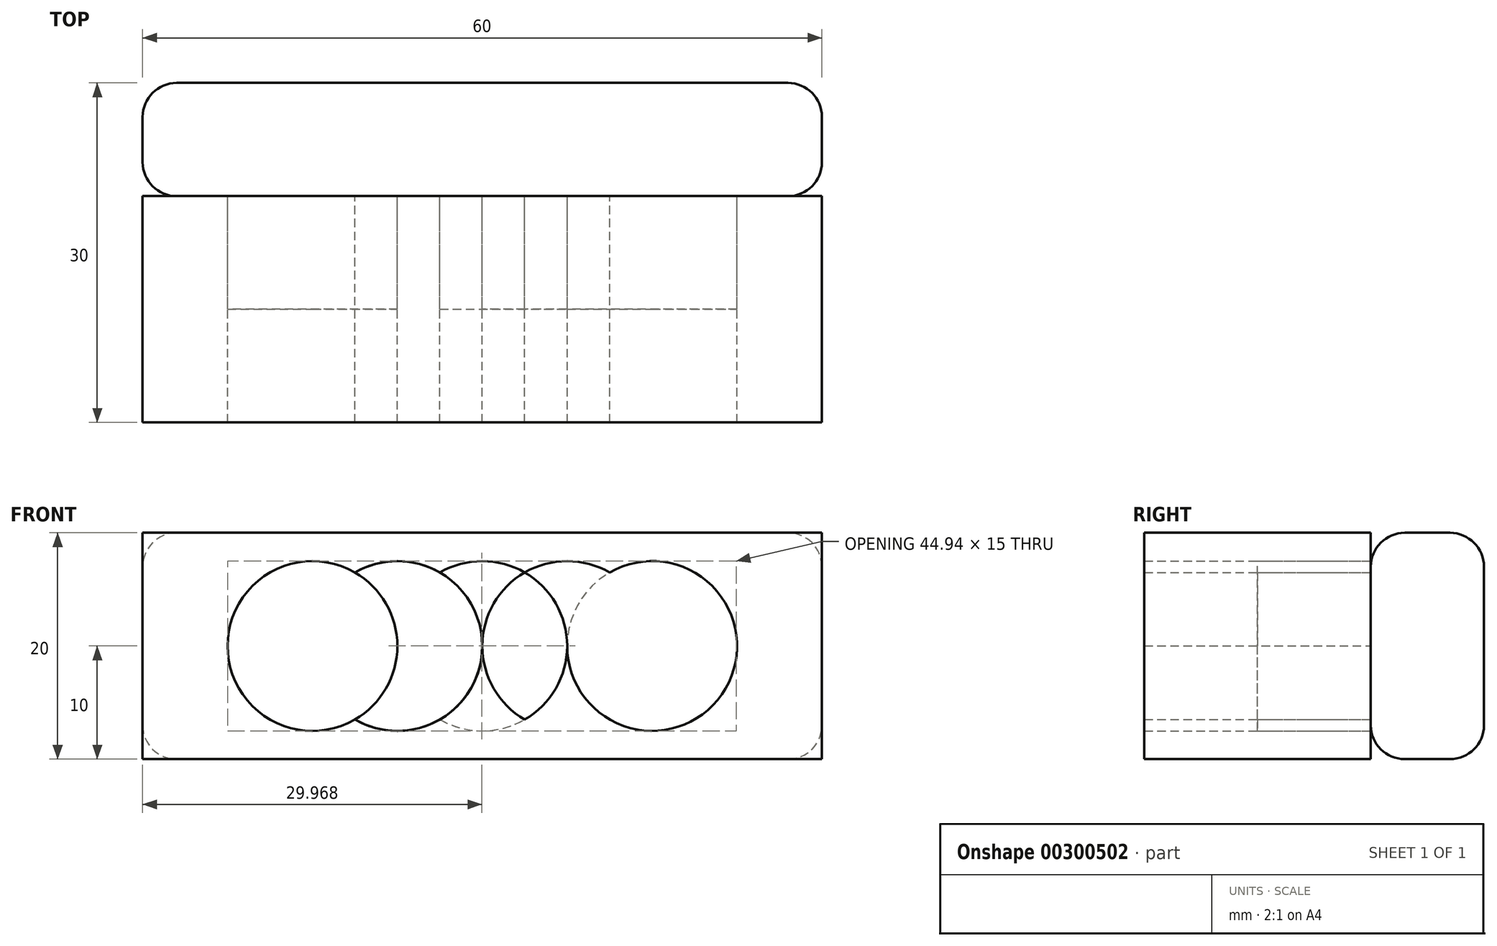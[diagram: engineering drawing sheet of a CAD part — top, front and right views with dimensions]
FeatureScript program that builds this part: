
annotation { "Feature Type Name" : "Feature", "Feature Type Description" : "" }
export const myFeature = defineFeature(function(context is Context, id is Id, definition is map)
    precondition{}
    {
        {
            var Q0;
            Q0=qCreatedBy(makeId("Front.planeOp"),FACE);
            var sketch = newSketch(context, id + "F0", { "sketchPlane" : qUnion([Q0])});
            skLineSegment(sketch, "E0.bottom", {"start": v(-30, 10) * mm, "end": v(30, 10) * mm});
            skLineSegment(sketch, "E0.top", {"start": v(-30, -10) * mm, "end": v(30, -10) * mm});
            skLineSegment(sketch, "E0.left", {"start": v(-30, 10) * mm, "end": v(-30, -10) * mm});
            skLineSegment(sketch, "E0.right", {"start": v(30, 10) * mm, "end": v(30, -10) * mm});
            skPoint(sketch, "E0.middle", {"position": v(0, 0) * mm});
            skSolve(sketch);
        }
        {
            var Q0;
            Q0=makeQuery(id+"F0.imprint","IMPRINT",FACE,{"disambiguationData":[TD([[makeQuery(id+"F0.imprint","IMPRINT",EDGE,{"derivedFrom":sQuery(id+"F0.wireOp",EDGE,"E0.bottom")}),-1.0]])]});
            extrude(context, id + "F1", {"entities" : qUnion([Q0]), "depth" : 10 * mm});
        }
        {
            var Q0;
            Q0=makeQuery(id+"F1.opExtrude","CAP_FACE",FACE,{"disambiguationData":[OSD([sQuery(id+"F0.wireOp",EDGE,"E0.bottom"),sQuery(id+"F0.wireOp",EDGE,"E0.top"),sQuery(id+"F0.wireOp",EDGE,"E0.left"),sQuery(id+"F0.wireOp",EDGE,"E0.right")])],"isStart":false});
            var sketch = newSketch(context, id + "F2", { "sketchPlane" : qUnion([Q0])});
            skCircle(sketch, "E1", {"center": v(0, 0) * mm, "radius": 7.5 * mm});
            skCircle(sketch, "E2", {"center": v(-7.5, 0) * mm, "radius": 7.5 * mm});
            skCircle(sketch, "E3", {"center": v(7.5, 0) * mm, "radius": 7.5 * mm});
            skCircle(sketch, "E4", {"center": v(15, 0) * mm, "radius": 7.5 * mm});
            skCircle(sketch, "E5", {"center": v(-15, 0) * mm, "radius": 7.5 * mm});
            skSolve(sketch);
        }
        {
            var Q0;
            {var subQ0=sQuery(id+"F2.wireOp",EDGE,"E5");var subQ1=sQuery(id+"F2.wireOp",EDGE,"E2");var subQ2=makeQuery(id+"F2.imprint","INTERSECT",VERTEX,{"disambiguationData":[OD(0.0)],"derivedFrom":[subQ1,subQ0]});Q0=makeQuery(id+"F2.imprint","IMPRINT",FACE,{"disambiguationData":[TD([[makeQuery(id+"F2.imprint","IMPRINT",EDGE,{"disambiguationData":[TD([[subQ2,-1.0]])],"derivedFrom":subQ1}),-1.0]])]});}
            var Q1;
            {var subQ0=sQuery(id+"F2.wireOp",EDGE,"E5");var subQ1=sQuery(id+"F2.wireOp",EDGE,"E2");var subQ2=makeQuery(id+"F2.imprint","INTERSECT",VERTEX,{"disambiguationData":[OD(0.0)],"derivedFrom":[subQ1,subQ0]});Q1=makeQuery(id+"F2.imprint","IMPRINT",FACE,{"disambiguationData":[TD([[makeQuery(id+"F2.imprint","IMPRINT",EDGE,{"disambiguationData":[TD([[subQ2,-1.0]])],"derivedFrom":subQ1}),1.0]])]});}
            var Q2;
            Q2=sQuery(id+"F2.wireOp",EDGE,"E5");
            var Q3;
            Q3=sQuery(id+"F2.wireOp",EDGE,"E4");
            extrude(context, id + "F3", {"entities" : qUnion([Q0, Q1]), "surfaceEntities" : qUnion([Q2, Q3]), "depth" : 10 * mm});
        }
        {
            var Q0;
            {var subQ0=sQuery(id+"F2.wireOp",EDGE,"E2");var subQ1=sQuery(id+"F2.wireOp",EDGE,"E1");var subQ2=makeQuery(id+"F2.imprint","INTERSECT",VERTEX,{"disambiguationData":[OD(0.0)],"derivedFrom":[subQ1,subQ0]});Q0=makeQuery(id+"F2.imprint","IMPRINT",FACE,{"disambiguationData":[TD([[makeQuery(id+"F2.imprint","IMPRINT",EDGE,{"disambiguationData":[TD([[subQ2,-1.0]])],"derivedFrom":subQ1}),1.0]])]});}
            var Q1;
            {var subQ0=sQuery(id+"F2.wireOp",EDGE,"E5");var subQ1=sQuery(id+"F2.wireOp",EDGE,"E1");var subQ2=makeQuery(id+"F2.imprint","INTERSECT",VERTEX,{"derivedFrom":[subQ1,subQ0]});Q1=makeQuery(id+"F2.imprint","IMPRINT",FACE,{"disambiguationData":[TD([[makeQuery(id+"F2.imprint","IMPRINT",EDGE,{"disambiguationData":[TD([[subQ2,-1.0]])],"derivedFrom":subQ1}),-1.0]])]});}
            var Q2;
            {var subQ0=sQuery(id+"F2.wireOp",EDGE,"E2");var subQ1=sQuery(id+"F2.wireOp",EDGE,"E1");var subQ2=makeQuery(id+"F2.imprint","INTERSECT",VERTEX,{"disambiguationData":[OD(0.0)],"derivedFrom":[subQ1,subQ0]});Q2=makeQuery(id+"F2.imprint","IMPRINT",FACE,{"disambiguationData":[TD([[makeQuery(id+"F2.imprint","IMPRINT",EDGE,{"disambiguationData":[TD([[subQ2,-1.0]])],"derivedFrom":subQ1}),-1.0]])]});}
            var Q3;
            Q3=sQuery(id+"F2.wireOp",EDGE,"E2");
            extrude(context, id + "F4", {"entities" : qUnion([Q0, Q1, Q2]), "surfaceEntities" : qUnion([Q3]), "depth" : 20 * mm});
        }
        {
            var Q0;
            {var subQ0=sQuery(id+"F2.wireOp",EDGE,"E3");var subQ1=sQuery(id+"F2.wireOp",EDGE,"E1");var subQ2=makeQuery(id+"F2.imprint","INTERSECT",VERTEX,{"disambiguationData":[OD(0.0)],"derivedFrom":[subQ1,subQ0]});Q0=makeQuery(id+"F2.imprint","IMPRINT",FACE,{"disambiguationData":[TD([[makeQuery(id+"F2.imprint","IMPRINT",EDGE,{"disambiguationData":[TD([[subQ2,1.0]])],"derivedFrom":subQ1}),1.0]])]});}
            var Q1;
            {var subQ0=sQuery(id+"F2.wireOp",EDGE,"E4");var subQ1=sQuery(id+"F2.wireOp",EDGE,"E1");var subQ2=makeQuery(id+"F2.imprint","INTERSECT",VERTEX,{"derivedFrom":[subQ1,subQ0]});Q1=makeQuery(id+"F2.imprint","IMPRINT",FACE,{"disambiguationData":[TD([[makeQuery(id+"F2.imprint","IMPRINT",EDGE,{"disambiguationData":[TD([[subQ2,1.0]])],"derivedFrom":subQ1}),-1.0]])]});}
            var Q2;
            {var subQ0=sQuery(id+"F2.wireOp",EDGE,"E3");var subQ1=sQuery(id+"F2.wireOp",EDGE,"E1");var subQ2=makeQuery(id+"F2.imprint","INTERSECT",VERTEX,{"disambiguationData":[OD(0.0)],"derivedFrom":[subQ1,subQ0]});Q2=makeQuery(id+"F2.imprint","IMPRINT",FACE,{"disambiguationData":[TD([[makeQuery(id+"F2.imprint","IMPRINT",EDGE,{"disambiguationData":[TD([[subQ2,1.0]])],"derivedFrom":subQ1}),-1.0]])]});}
            var Q3;
            Q3=sQuery(id+"F2.wireOp",EDGE,"E3");
            extrude(context, id + "F5", {"entities" : qUnion([Q0, Q1, Q2]), "surfaceEntities" : qUnion([Q3]), "depth" : 20 * mm});
        }
        {
            var Q0;
            {var subQ0=sQuery(id+"F2.wireOp",EDGE,"E2");var subQ1=sQuery(id+"F2.wireOp",EDGE,"E1");var subQ2=makeQuery(id+"F2.imprint","INTERSECT",VERTEX,{"disambiguationData":[OD(1.0)],"derivedFrom":[subQ1,subQ0]});Q0=makeQuery(id+"F2.imprint","IMPRINT",FACE,{"disambiguationData":[TD([[makeQuery(id+"F2.imprint","IMPRINT",EDGE,{"disambiguationData":[TD([[subQ2,-1.0]])],"derivedFrom":subQ1}),1.0]])]});}
            var Q1;
            {var subQ0=sQuery(id+"F2.wireOp",EDGE,"E3");var subQ1=sQuery(id+"F2.wireOp",EDGE,"E1");var subQ2=makeQuery(id+"F2.imprint","INTERSECT",VERTEX,{"disambiguationData":[OD(0.0)],"derivedFrom":[subQ1,subQ0]});Q1=makeQuery(id+"F2.imprint","IMPRINT",FACE,{"disambiguationData":[TD([[makeQuery(id+"F2.imprint","IMPRINT",EDGE,{"disambiguationData":[TD([[subQ2,-1.0]])],"derivedFrom":subQ1}),1.0]])]});}
            var Q2;
            {var subQ0=sQuery(id+"F2.wireOp",EDGE,"E4");var subQ1=sQuery(id+"F2.wireOp",EDGE,"E3");var subQ2=makeQuery(id+"F2.imprint","INTERSECT",VERTEX,{"disambiguationData":[OD(0.0)],"derivedFrom":[subQ1,subQ0]});Q2=makeQuery(id+"F2.imprint","IMPRINT",FACE,{"disambiguationData":[TD([[makeQuery(id+"F2.imprint","IMPRINT",EDGE,{"disambiguationData":[TD([[subQ2,1.0]])],"derivedFrom":subQ1}),1.0]])]});}
            var Q3;
            {var subQ0=sQuery(id+"F2.wireOp",EDGE,"E4");var subQ1=sQuery(id+"F2.wireOp",EDGE,"E3");var subQ2=makeQuery(id+"F2.imprint","INTERSECT",VERTEX,{"disambiguationData":[OD(0.0)],"derivedFrom":[subQ1,subQ0]});Q3=makeQuery(id+"F2.imprint","IMPRINT",FACE,{"disambiguationData":[TD([[makeQuery(id+"F2.imprint","IMPRINT",EDGE,{"disambiguationData":[TD([[subQ2,1.0]])],"derivedFrom":subQ1}),-1.0]])]});}
            var Q4;
            Q4=sQuery(id+"F2.wireOp",EDGE,"E1");
            extrude(context, id + "F6", {"entities" : qUnion([Q0, Q1, Q2, Q3]), "surfaceEntities" : qUnion([Q4]), "depth" : 10 * mm});
        }
        {
            var Q0;
            Q0=makeQuery(id+"F1.opExtrude","CAP_EDGE",EDGE,{"disambiguationData":[OSD([sQuery(id+"F0.wireOp",EDGE,"E0.left")])],"isStart":false});
            var Q1;
            Q1=makeQuery(id+"F1.opExtrude","CAP_FACE",FACE,{"disambiguationData":[OSD([sQuery(id+"F0.wireOp",EDGE,"E0.bottom"),sQuery(id+"F0.wireOp",EDGE,"E0.top"),sQuery(id+"F0.wireOp",EDGE,"E0.left"),sQuery(id+"F0.wireOp",EDGE,"E0.right")])],"isStart":false});
            var Q2;
            Q2=makeQuery(id+"F1.opExtrude","SWEPT_FACE",FACE,{"disambiguationData":[OSD([sQuery(id+"F0.wireOp",EDGE,"E0.top")])]});
            var Q3;
            Q3=makeQuery(id+"F1.opExtrude","SWEPT_FACE",FACE,{"disambiguationData":[OSD([sQuery(id+"F0.wireOp",EDGE,"E0.left")])]});
            var Q4;
            Q4=makeQuery(id+"F1.opExtrude","CAP_FACE",FACE,{"disambiguationData":[OSD([sQuery(id+"F0.wireOp",EDGE,"E0.bottom"),sQuery(id+"F0.wireOp",EDGE,"E0.top"),sQuery(id+"F0.wireOp",EDGE,"E0.left"),sQuery(id+"F0.wireOp",EDGE,"E0.right")])],"isStart":true});
            var Q5;
            Q5=makeQuery(id+"F1.opExtrude","SWEPT_FACE",FACE,{"disambiguationData":[OSD([sQuery(id+"F0.wireOp",EDGE,"E0.bottom")])]});
            var Q6;
            Q6=makeQuery(id+"F1.opExtrude","SWEPT_FACE",FACE,{"disambiguationData":[OSD([sQuery(id+"F0.wireOp",EDGE,"E0.right")])]});
            fillet(context, id + "F7", {"entities" : qUnion([Q0, Q1, Q2, Q3, Q4, Q5, Q6]), "radius" : 3 * mm, "tangentPropagation" : true, "allowEdgeOverflow" : false});
        }
    });
